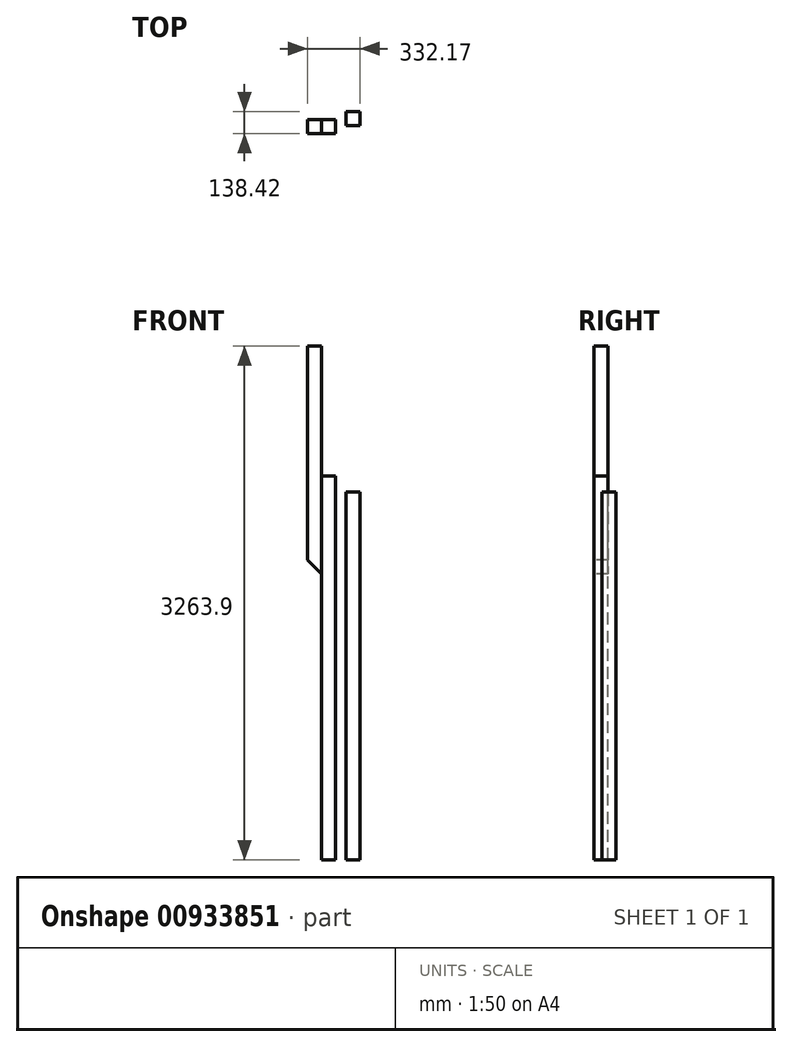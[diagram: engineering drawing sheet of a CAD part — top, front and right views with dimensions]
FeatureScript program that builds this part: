
annotation { "Feature Type Name" : "Feature", "Feature Type Description" : "" }
export const myFeature = defineFeature(function(context is Context, id is Id, definition is map)
    precondition{}
    {
        {
            var Q0;
            Q0=qCreatedBy(makeId("Front.planeOp"),FACE);
            var sketch = newSketch(context, id + "F0", { "sketchPlane" : qUnion([Q0])});
            skLineSegment(sketch, "E0.bottom", {"start": v(-155.62, 0) * mm, "end": v(-66.72, 0) * mm});
            skLineSegment(sketch, "E0.top", {"start": v(-155.62, 2438.4) * mm, "end": v(-66.72, 2438.4) * mm});
            skLineSegment(sketch, "E0.left", {"start": v(-155.62, 0) * mm, "end": v(-155.62, 2438.4) * mm});
            skLineSegment(sketch, "E0.right", {"start": v(-66.72, 0) * mm, "end": v(-66.72, 2438.4) * mm});
            skSolve(sketch);
        }
        {
            var Q0;
            Q0=qSketchRegion(id+"F0",true);
            extrude(context, id + "F1", {"entities" : qUnion([Q0]), "depth" : 88.9 * mm});
        }
        {
            var Q0;
            Q0=makeQuery(id+"F1.opExtrude","CAP_FACE",FACE,{"disambiguationData":[OSD([sQuery(id+"F0.wireOp",EDGE,"E0.bottom"),sQuery(id+"F0.wireOp",EDGE,"E0.top"),sQuery(id+"F0.wireOp",EDGE,"E0.left"),sQuery(id+"F0.wireOp",EDGE,"E0.right")])],"isStart":false});
            var sketch = newSketch(context, id + "F2", { "sketchPlane" : qUnion([Q0])});
            skLineSegment(sketch, "E1", {"start": v(-155.62, 1816.1) * mm, "end": v(-155.62, 3263.9) * mm});
            skLineSegment(sketch, "E2", {"start": v(-155.62, 3263.9) * mm, "end": v(-244.52, 3263.9) * mm});
            skLineSegment(sketch, "E3", {"start": v(-244.52, 3263.9) * mm, "end": v(-244.52, 1905) * mm});
            skLineSegment(sketch, "E4", {"start": v(-244.52, 1905) * mm, "end": v(-155.62, 1816.1) * mm});
            skSolve(sketch);
        }
        {
            var Q0;
            Q0=qSketchRegion(id+"F2",true);
            var Q1;
            Q1=makeQuery(id+"F1.opExtrude","CAP_FACE",FACE,{"disambiguationData":[OSD([sQuery(id+"F0.wireOp",EDGE,"E0.bottom"),sQuery(id+"F0.wireOp",EDGE,"E0.top"),sQuery(id+"F0.wireOp",EDGE,"E0.left"),sQuery(id+"F0.wireOp",EDGE,"E0.right")])],"isStart":true});
            extrude(context, id + "F3", {"entities" : qUnion([Q0]), "endBound" : BoundingType.UP_TO_SURFACE, "oppositeDirection" : true, "endBoundEntityFace" : qUnion([Q1]), "depth" : 25.4 * mm});
        }
        {
            var Q0;
            Q0=qCreatedBy(makeId("Top.planeOp"),FACE);
            var sketch = newSketch(context, id + "F4", { "sketchPlane" : qUnion([Q0])});
            skLineSegment(sketch, "E5.bottom", {"start": v(-1.25, 49.52) * mm, "end": v(87.65, 49.52) * mm});
            skLineSegment(sketch, "E5.top", {"start": v(-1.25, -39.38) * mm, "end": v(87.65, -39.38) * mm});
            skLineSegment(sketch, "E5.left", {"start": v(-1.25, 49.52) * mm, "end": v(-1.25, -39.38) * mm});
            skLineSegment(sketch, "E5.right", {"start": v(87.65, 49.52) * mm, "end": v(87.65, -39.38) * mm});
            skSolve(sketch);
        }
        {
            var Q0;
            Q0=qSketchRegion(id+"F4",true);
            extrude(context, id + "F5", {"entities" : qUnion([Q0]), "depth" : 2336.8 * mm});
        }
    });
